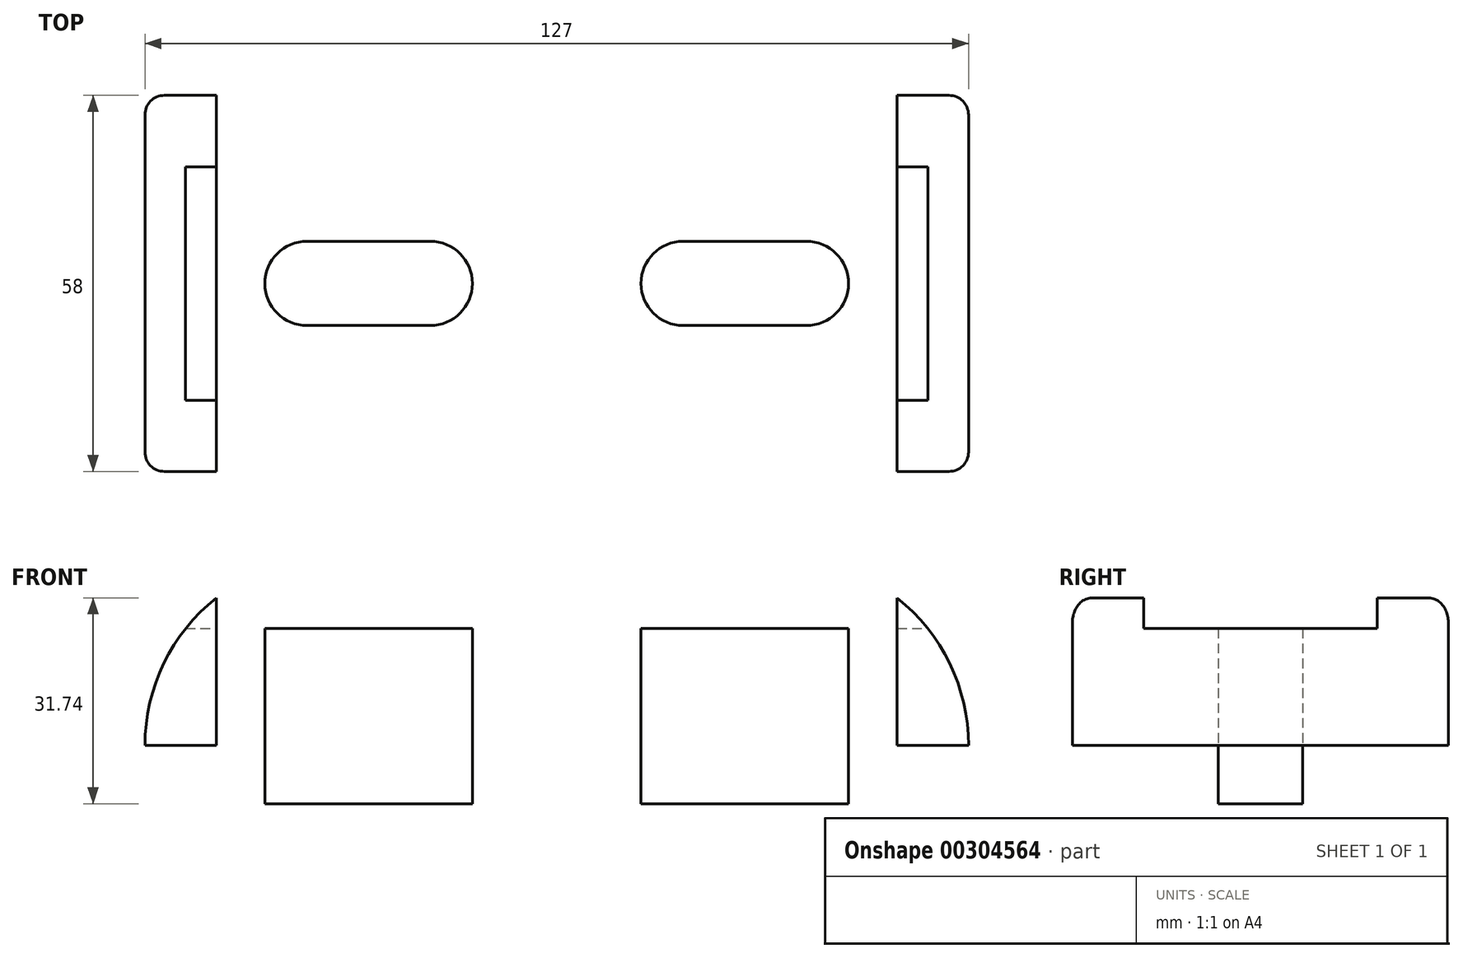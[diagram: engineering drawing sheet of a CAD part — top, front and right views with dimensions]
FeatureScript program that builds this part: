
annotation { "Feature Type Name" : "Feature", "Feature Type Description" : "" }
export const myFeature = defineFeature(function(context is Context, id is Id, definition is map)
    precondition{}
    {
        {
            var Q0;
            Q0=qCreatedBy(makeId("Front.planeOp"),FACE);
            var sketch = newSketch(context, id + "F0", { "sketchPlane" : qUnion([Q0])});
            skLineSegment(sketch, "E0", {"start": v(0, 0) * mm, "end": v(0, 9) * mm});
            skLineSegment(sketch, "E1", {"start": v(0, 9) * mm, "end": v(-11, 9) * mm});
            skLineSegment(sketch, "E2", {"start": v(0, 0) * mm, "end": v(105, 0) * mm});
            skLineSegment(sketch, "E3", {"start": v(105, 0) * mm, "end": v(105, 9) * mm});
            skLineSegment(sketch, "E4", {"start": v(116, 9) * mm, "end": v(105, 9) * mm});
            skLineSegment(sketch, "E5", {"start": v(18, 38) * mm, "end": v(87, 38) * mm});
            skArc(sketch, "E6", {"start": v(18, 38) * mm, "mid": v(-2.5, 29.5) * mm, "end": v(-11, 9) * mm});
            skArc(sketch, "E7", {"start": v(116, 9) * mm, "mid": v(107.5, 29.5) * mm, "end": v(87, 38) * mm});
            skSolve(sketch);
        }
        {
            var Q0;
            Q0=makeQuery(id+"F0.imprint","IMPRINT",FACE,{"disambiguationData":[TD([[makeQuery(id+"F0.imprint","IMPRINT",EDGE,{"derivedFrom":sQuery(id+"F0.wireOp",EDGE,"E0")}),-1.0]])]});
            extrude(context, id + "F1", {"entities" : qUnion([Q0]), "depth" : 58 * mm, "symmetric" : true});
        }
        {
            var Q0;
            Q0=makeQuery(id+"F1.opExtrude","CAP_FACE",FACE,{"disambiguationData":[OSD([sQuery(id+"F0.wireOp",EDGE,"E0"),sQuery(id+"F0.wireOp",EDGE,"E1"),sQuery(id+"F0.wireOp",EDGE,"E2"),sQuery(id+"F0.wireOp",EDGE,"E3"),sQuery(id+"F0.wireOp",EDGE,"E4"),sQuery(id+"F0.wireOp",EDGE,"E5"),sQuery(id+"F0.wireOp",EDGE,"E6"),sQuery(id+"F0.wireOp",EDGE,"E7")])],"isStart":false});
            var sketch = newSketch(context, id + "F2", { "sketchPlane" : qUnion([Q0])});
            skLineSegment(sketch, "E8", {"start": v(-4.74, 27) * mm, "end": v(109.74, 27) * mm});
            skArc(sketch, "E9", {"start": v(18, 38) * mm, "mid": v(5.37, 35.1) * mm, "end": v(-4.74, 27) * mm});
            skArc(sketch, "E10", {"start": v(109.74, 27) * mm, "mid": v(99.63, 35.1) * mm, "end": v(87, 38) * mm});
            skLineSegment(sketch, "E11", {"start": v(18, 38) * mm, "end": v(87, 38) * mm});
            skSolve(sketch);
        }
        {
            var Q0;
            Q0=makeQuery(id+"F2.imprint","IMPRINT",FACE,{"disambiguationData":[TD([[makeQuery(id+"F2.imprint","IMPRINT",EDGE,{"derivedFrom":sQuery(id+"F2.wireOp",EDGE,"E8")}),1.0]])]});
            extrude(context, id + "F3", {"entities" : qUnion([Q0]), "operationType" : NewBodyOperationType.REMOVE, "oppositeDirection" : true, "depth" : 47 * mm, "hasSecondDirection" : true, "secondDirectionOppositeDirection" : true, "secondDirectionDepth" : 11 * mm});
        }
        {
            var Q0;
            Q0=makeQuery(id+"F1.opExtrude","CAP_EDGE",EDGE,{"disambiguationData":[OSD([sQuery(id+"F0.wireOp",EDGE,"E5")])],"isStart":false});
            var Q1;
            Q1=makeQuery(id+"F1.opExtrude","CAP_EDGE",EDGE,{"disambiguationData":[OSD([sQuery(id+"F0.wireOp",EDGE,"E5")])],"isStart":true});
            fillet(context, id + "F4", {"entities" : qUnion([Q0, Q1]), "radius" : 3 * mm, "tangentPropagation" : true, "allowEdgeOverflow" : false});
        }
        {
            var Q0;
            Q0=makeQuery(id+"F1.opExtrude","SWEPT_FACE",FACE,{"disambiguationData":[OSD([sQuery(id+"F0.wireOp",EDGE,"E2")])]});
            var sketch = newSketch(context, id + "F5", { "sketchPlane" : qUnion([Q0])});
            skLineSegment(sketch, "E12", {"start": v(14, 0) * mm, "end": v(33, 0) * mm, "construction": true});
            skLineSegment(sketch, "E13", {"start": v(72, 0) * mm, "end": v(91, 0) * mm, "construction": true});
            skArc(sketch, "E14.0.startCap", {"start": v(14, -6.5) * mm, "mid": v(7.5, 0) * mm, "end": v(14, 6.5) * mm});
            skArc(sketch, "E14.0.endCap", {"start": v(33, 6.5) * mm, "mid": v(39.5, 0) * mm, "end": v(33, -6.5) * mm});
            skLineSegment(sketch, "E14.0.left", {"start": v(14, 6.5) * mm, "end": v(33, 6.5) * mm});
            skLineSegment(sketch, "E14.0.right", {"start": v(14, -6.5) * mm, "end": v(33, -6.5) * mm});
            skArc(sketch, "E14.1.startCap", {"start": v(72, -6.5) * mm, "mid": v(65.5, 0) * mm, "end": v(72, 6.5) * mm});
            skArc(sketch, "E14.1.endCap", {"start": v(91, 6.5) * mm, "mid": v(97.5, 0) * mm, "end": v(91, -6.5) * mm});
            skLineSegment(sketch, "E14.1.left", {"start": v(72, 6.5) * mm, "end": v(91, 6.5) * mm});
            skLineSegment(sketch, "E14.1.right", {"start": v(72, -6.5) * mm, "end": v(91, -6.5) * mm});
            skSolve(sketch);
        }
        {
            var Q0;
            Q0=makeQuery(id+"F5.imprint","IMPRINT",FACE,{"disambiguationData":[TD([[makeQuery(id+"F5.imprint","IMPRINT",EDGE,{"derivedFrom":sQuery(id+"F5.wireOp",EDGE,"E14.0.startCap")}),-1.0]])]});
            var Q1;
            Q1=makeQuery(id+"F5.imprint","IMPRINT",FACE,{"disambiguationData":[TD([[makeQuery(id+"F5.imprint","IMPRINT",EDGE,{"derivedFrom":sQuery(id+"F5.wireOp",EDGE,"E14.1.startCap")}),-1.0]])]});
            extrude(context, id + "F6", {"entities" : qUnion([Q0, Q1]), "operationType" : NewBodyOperationType.REMOVE, "endBound" : BoundingType.THROUGH_ALL, "oppositeDirection" : true, "depth" : 25 * mm});
        }
    });
